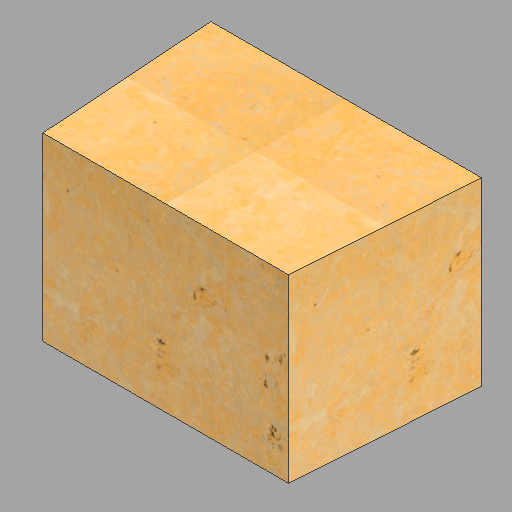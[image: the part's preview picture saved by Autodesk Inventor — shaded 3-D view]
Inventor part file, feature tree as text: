
AUTODESK INVENTOR PART (.ipt)
format: ipt  version: 2023 (Build 270158030, 158C)  size: 409,600 bytes
history: native  units: in
note: dims shown in document units (in); Inventor stores cm internally (conversion verified against a paired STEP export)
features: other x1, extrude x1, sketch x1
ambient origin geometry x8: Origin, YZ Plane, XZ Plane, XY Plane, X Axis, Y Axis, Z Axis, Center Point
bodies: Solid1 (feature_tree)
feature tree (3):
  other  "Boulder wall block - 20"
  extrude  "Extrusion1"  Depth=24.0in
  sketch  "Sketch1"  dims[d0=36.0in d1=24.0in d2=0.055in d3=24.0in d4=0.0in d5=24.0in]
